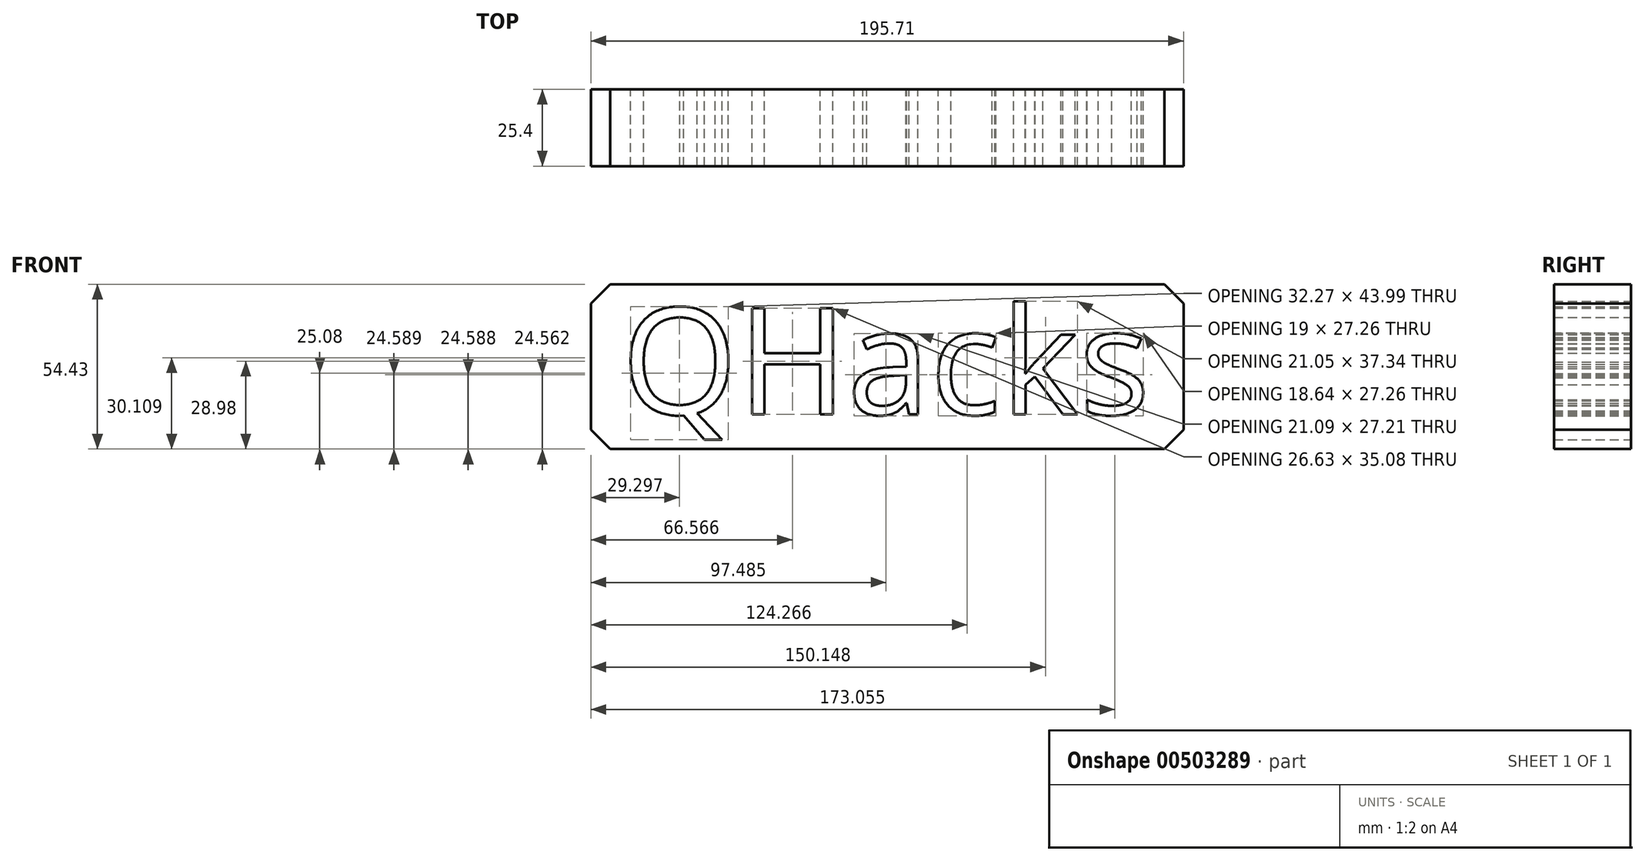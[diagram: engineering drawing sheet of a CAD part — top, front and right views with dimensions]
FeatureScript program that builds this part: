
annotation { "Feature Type Name" : "Feature", "Feature Type Description" : "" }
export const myFeature = defineFeature(function(context is Context, id is Id, definition is map)
    precondition{}
    {
        {
            var Q0;
            Q0=qCreatedBy(makeId("Front.planeOp"),FACE);
            var sketch = newSketch(context, id + "F0", { "sketchPlane" : qUnion([Q0])});
            skLineSegment(sketch, "E0.bottom", {"start": v(-96.26, 46.29) * mm, "end": v(99.45, 46.29) * mm});
            skLineSegment(sketch, "E0.top", {"start": v(-96.26, -8.14) * mm, "end": v(99.45, -8.14) * mm});
            skLineSegment(sketch, "E0.left", {"start": v(-96.26, 46.29) * mm, "end": v(-96.26, -8.14) * mm});
            skLineSegment(sketch, "E0.right", {"start": v(99.45, 46.29) * mm, "end": v(99.45, -8.14) * mm});
            skText(sketch, "E1", { "text": "QHacks", "fontName": "OpenSans-Regular.ttf"});
            const initialGuessF0  = {"E1": [-0.0861, 0.0033, 1, 0, 0.03538]};
            skSetInitialGuess(sketch, initialGuessF0);
            skSolve(sketch);
        }
        {
            var Q0;
            Q0=makeQuery(id+"F0.imprint","IMPRINT",FACE,{"disambiguationData":[TD([[makeQuery(id+"F0.imprint","IMPRINT",EDGE,{"derivedFrom":sQuery(id+"F0.wireOp",EDGE,"E0.bottom")}),-1.0]])]});
            var Q1;
            Q1=makeQuery(id+"F0.imprint","IMPRINT",FACE,{"disambiguationData":[TD([[makeQuery(id+"F0.imprint","IMPRINT",EDGE,{"derivedFrom":sQuery(id+"F0.wireOp",EDGE,"E1.sketch_text.stroke-12")}),1.0]])]});
            var Q2;
            Q2=makeQuery(id+"F0.imprint","IMPRINT",FACE,{"disambiguationData":[TD([[makeQuery(id+"F0.imprint","IMPRINT",EDGE,{"derivedFrom":sQuery(id+"F0.wireOp",EDGE,"E1.sketch_text.stroke-51")}),1.0]])]});
            extrude(context, id + "F1", {"entities" : qUnion([Q0, Q1, Q2]), "depth" : 25.4 * mm});
        }
        {
            var Q0;
            Q0=makeQuery(id+"F1.opExtrude","SWEPT_EDGE",EDGE,{"disambiguationData":[OSD([sQuery(id+"F0.wireOp",EDGE,"E0.bottom"),sQuery(id+"F0.wireOp",EDGE,"E0.left")])]});
            var Q1;
            Q1=makeQuery(id+"F1.opExtrude","SWEPT_EDGE",EDGE,{"disambiguationData":[OSD([sQuery(id+"F0.wireOp",EDGE,"E0.bottom"),sQuery(id+"F0.wireOp",EDGE,"E0.right")])]});
            var Q2;
            Q2=makeQuery(id+"F1.opExtrude","SWEPT_EDGE",EDGE,{"disambiguationData":[OSD([sQuery(id+"F0.wireOp",EDGE,"E0.top"),sQuery(id+"F0.wireOp",EDGE,"E0.right")])]});
            var Q3;
            Q3=makeQuery(id+"F1.opExtrude","SWEPT_EDGE",EDGE,{"disambiguationData":[OSD([sQuery(id+"F0.wireOp",EDGE,"E0.top"),sQuery(id+"F0.wireOp",EDGE,"E0.left")])]});
            chamfer(context, id + "F2", {"entities" : qUnion([Q0, Q1, Q2, Q3]), "width" : 6.35 * mm, "tangentPropagation" : true});
        }
    });
